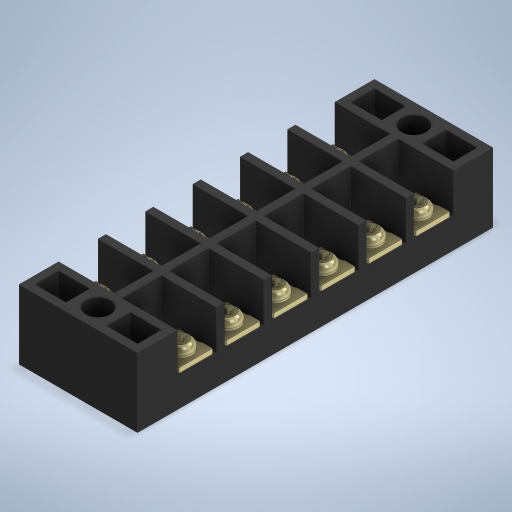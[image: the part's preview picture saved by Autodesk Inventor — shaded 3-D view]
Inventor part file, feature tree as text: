
AUTODESK INVENTOR PART (.ipt)
format: ipt  version: 2024 (Build 280153000, 153)  size: 2,169,856 bytes
history: native  units: in
note: dims shown in document units (in); Inventor stores cm internally (conversion verified against a paired STEP export)
features: sketch x9, extrude x7, plane x6, mirror x4, fillet x2, projected_geometry x1
ambient origin geometry x8: Origin, YZ Plane, XZ Plane, XY Plane, X Axis, Y Axis, Z Axis, Center Point
bodies: Solid1 (feature_tree)
feature tree (29):
  extrude  "Extrusion1"  Depth=3.6in
  extrude  "Extrusion2"  Depth=0.4in
  extrude  "Extrusion3"  Depth=0.4in
  extrude  "Extrusion4"  Depth=0.08in
  extrude  "Extrusion5"  Depth=0.08in
  fillet  "Fillet1"  Radius=0.4in
  extrude  "Extrusion6"  Depth=0.4in
  plane  "Work Plane1"
  plane  "Work Plane2"
  plane  "Work Plane3"
  plane  "Work Plane4"
  plane  "Work Plane5"
  plane  "Work Plane6"
  extrude  "Extrusion7"  Depth=0.4in
  fillet  "Fillet2"  Radius=0.08in
  mirror  "Mirror2"
  mirror  "Mirror3"
  mirror  "Mirror4"
  mirror  "Mirror5"
  sketch  "Sketch8"  dims[d17=0.04in]
  sketch  "Sketch9"  dims[d18=0.08in d19=0.4in d20=0.0in d21=0.25in d22=0.08in d23=0.08in d24=0.4in d25=0.0in d26=0.17in d27=0.34in d28=0.35in d29=0.34in d30=0.01in d31=0.01in d32=0.05in d33=0.0in d34=0.1in d35=0.0in d36=0.08in d37=0.01in d38=0.0in d39=-0.04in d40=-0.04in d41=-0.04in d42=-0.04in d43=-0.04in d44=-0.04in d45=0.095in d46=0.095in d47=0.045in d48=0.09in d49=0.02in d50=0.02in d51=0.02in d52=0.02in d53=0.02in d54=0.04in d55=0.06in d56=0.0in d57=0.005in]
  sketch  "Sketch1"  dims[d0=1.2in d1=3.6in]
  sketch  "Sketch2"  dims[d2=0.7in d3=0.0in d4=0.4in]
  sketch  "Sketch3"  dims[d5=0.4in d6=0.4in]
  sketch  "Sketch4"  dims[d7=0.4in d8=0.08in]
  sketch  "Sketch5"  dims[d9=0.4in d10=0.08in d11=0.4in]
  sketch  "Sketch6"  dims[d12=0.08in d13=0.4in]
  sketch  "Sketch7"  dims[d14=0.08in d15=0.4in d16=0.08in]
  projected_geometry  "Projected Loop1"
